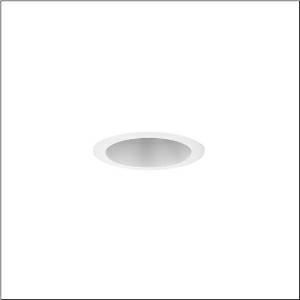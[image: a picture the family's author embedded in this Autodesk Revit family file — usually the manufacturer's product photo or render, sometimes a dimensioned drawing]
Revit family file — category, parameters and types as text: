
# Revit family: lunis_31_mini_51dn157e31
name_source: partatom
category: Lighting Fixtures
units: mm (PartAtom-declared; Revit-internal decimal feet)

## family parameters
Cut with Voids When Loaded = No
Host = Face
Light Source = No
Part Type = Normal
Room Calculation Point = No
Round Connector Dimension = Use Diameter
Shared = No

## types (1)
- Lunis 31 mini (1 x LED, 1000 lm, 8.3 W, 3000K)
    Apparent Load = 8 VA
    CIE Flux Codes = 93 98 100 100 100
    Color Rendering = 80
    Color Temperature = 3000K
    Default Elevation = 1800 mm
    Description = Lunis 31,  mini, downlight, light control with reflector, light emission: direct distribution, LED rated luminous flux: 1.000lm, light colour: 830, control gear: ECG, mains connection: 220..240V, AC, 50/60Hz, housing, white, protection rating (complete): IP20, insulation class (complete): insulation class II (safety insulation), certification: CE, packaging unit: 1 piece
    Height = 0 mm  [stored 0 ft]
    Lamp = 1 x LED
    Lamp Light Flux = 1000 lm
    Lamp Power = 8.3 W
    Lamp count = 1
    Length = 188 mm  [stored 0.616798 ft]
    Luminous efficacy = 120 lm/W
    Manufacturer = Siteco
    ModVariant = No
    Model = 51DN157E31
    Mounting Place = Ceiling
    Mounting Type = Recessed
    Number of Poles = 1
    OnlyDefault = Yes
    Power Factor = 1
    Product Name = Lunis 31 mini
    Product group = downlight | ceiling recessed
    ProductGroupID = 402
    Protection Class = Protection class II
    Protection Degree = IP 20
    RLX_Detail_Level = 1
    RlxData = <blob elided: 21905 chars, md5=4f2d2e13>
    Socket = socket
    Standby Power = 0 W
    System Light Flux = 1000 lm
    System Power = 8 W
    Type Comments = Product without accessories
    Type Image = l_1005624.jpg
    URL = http://relux.com
    VarID = ---
    Voltage = 0 V
    Weight = 0.00 kg
    Width = 0 mm  [stored 0 ft]

note: [stored X ft] marks values corroborated as IEEE doubles in the binary element streams (Revit-internal decimal feet)

## geometry (parser evidence)
native form markers: Blend x4, Sweep x11
no freeform markers — native parametric forms only
